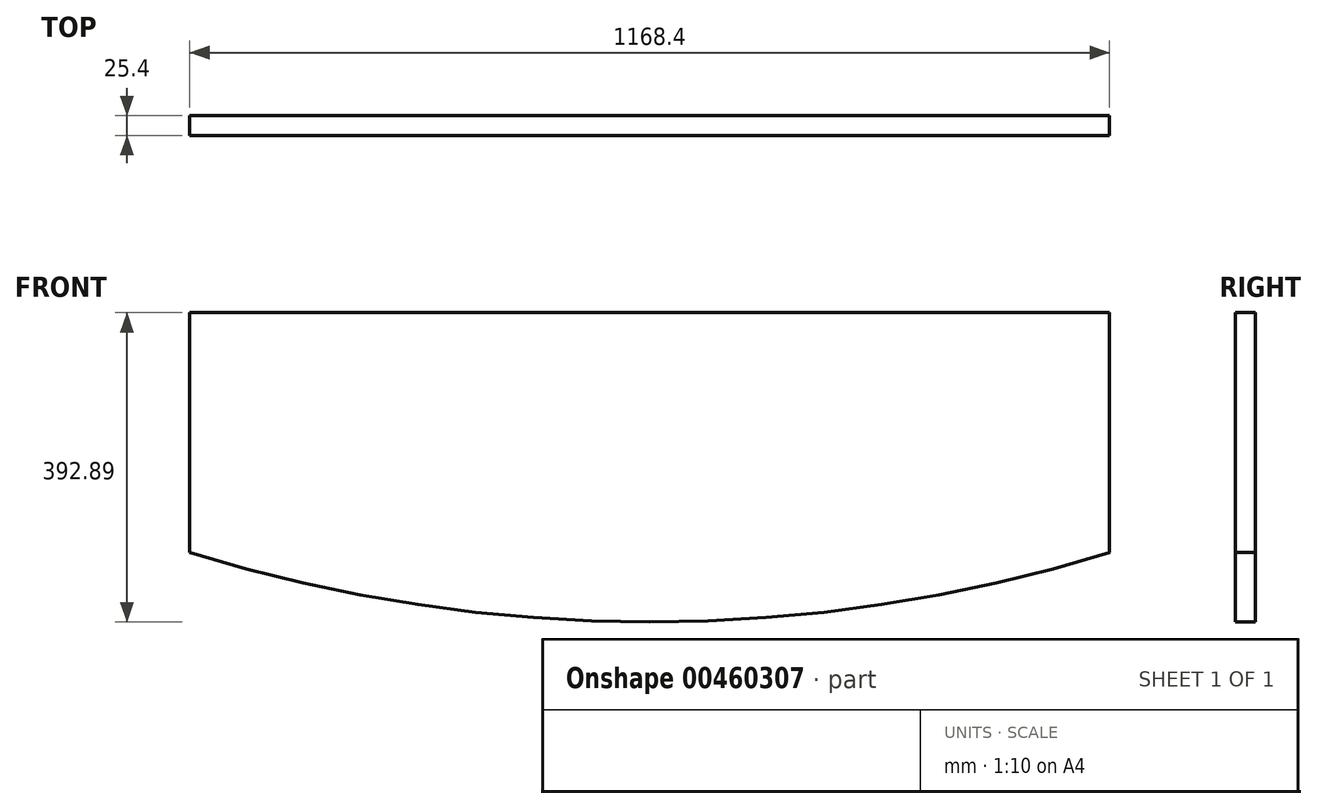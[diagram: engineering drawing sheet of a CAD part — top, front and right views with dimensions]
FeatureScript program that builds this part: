
annotation { "Feature Type Name" : "Feature", "Feature Type Description" : "" }
export const myFeature = defineFeature(function(context is Context, id is Id, definition is map)
    precondition{}
    {
        {
            var Q0;
            Q0=qCreatedBy(makeId("Front.planeOp"),FACE);
            var sketch = newSketch(context, id + "F0", { "sketchPlane" : qUnion([Q0])});
            skLineSegment(sketch, "E0.bottom", {"start": v(-584.2, 152.4) * mm, "end": v(584.2, 152.4) * mm});
            skLineSegment(sketch, "E0.left", {"start": v(-584.2, 152.4) * mm, "end": v(-584.2, -152.4) * mm});
            skLineSegment(sketch, "E0.right", {"start": v(584.2, 152.4) * mm, "end": v(584.2, -152.4) * mm});
            skArc(sketch, "E1", {"start": v(-584.2, -152.4) * mm, "mid": v(0, -240.5) * mm, "end": v(584.2, -152.4) * mm});
            skSolve(sketch);
        }
        {
            var Q0;
            Q0 = qSketchRegion(id + "F0", true);
            extrude(context, id + "F1", {"entities" : qUnion([Q0]), "depth" : 25.4 * mm});
        }
    });
